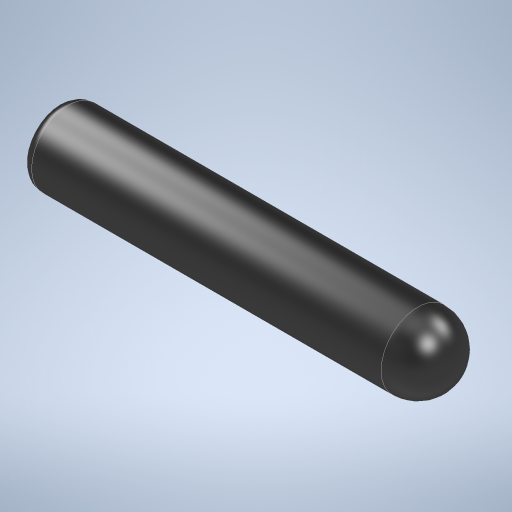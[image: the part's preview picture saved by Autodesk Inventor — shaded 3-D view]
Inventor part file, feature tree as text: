
AUTODESK INVENTOR PART (.ipt)
format: ipt  version: 2024 (Build 280153000, 153)  size: 257,536 bytes
history: native  units: mm
features: revolve x1, fillet x1, sketch x1
ambient origin geometry x8: Origin, YZ Plane, XZ Plane, XY Plane, X Axis, Y Axis, Z Axis, Center Point
bodies: Volumenkörper1 (feature_tree)
feature tree (3):
  revolve  "Umdrehung1"
  fillet  "Rundung1"  Radius=49.0mm
  sketch  "Skizze1"  dims[d1=10.0mm d2=90.0deg d6=1.5mm]
